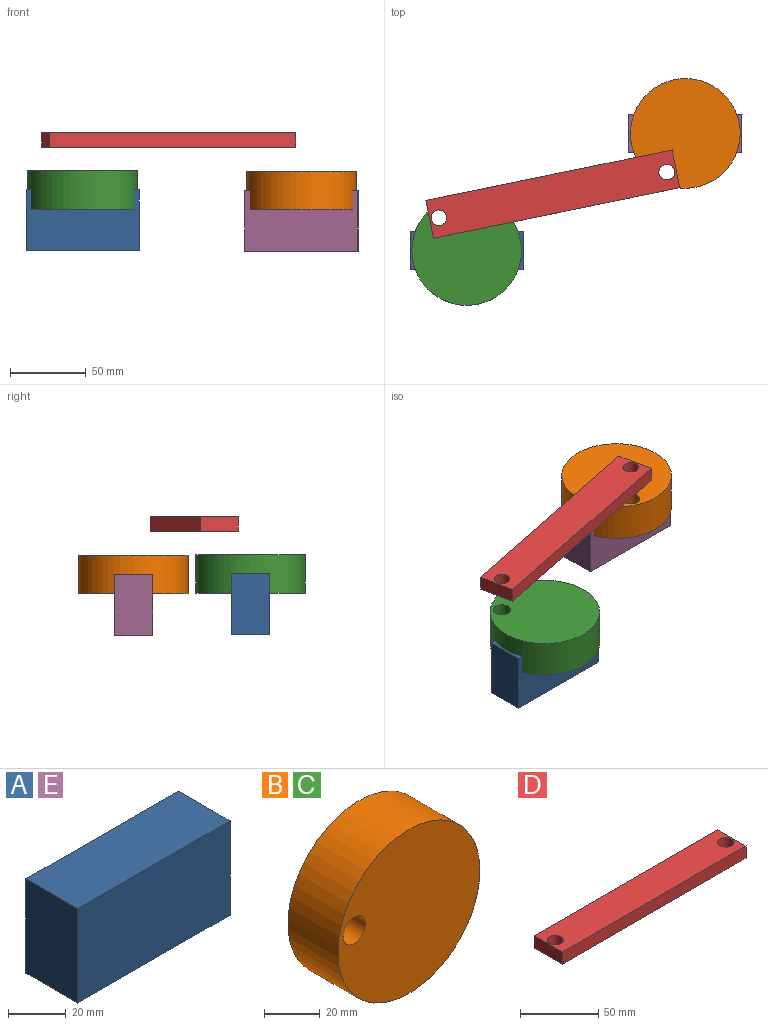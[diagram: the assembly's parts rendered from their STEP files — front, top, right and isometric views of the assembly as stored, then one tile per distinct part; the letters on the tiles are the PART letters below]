
ASSEMBLY  parts=5 mates=4
PART A: 6 faces, bbox 74.7x25.4x40 mm
  f0: plane 40.01x25.4mm, normal (-1,0,0), area 1016.1mm2, adj f1,f3,f4,f5
  f1: plane 74.7x25.4mm, normal (0,0,-1), area 1897.4mm2, adj f0,f2,f4,f5
  f2: plane 40.01x25.4mm, normal (1,0,0), area 1016.1mm2, adj f1,f3,f4,f5
  f3: plane 74.7x25.4mm, normal (0,0,1), area 1897.4mm2, adj f0,f2,f4,f5
  f4: plane 74.7x40.01mm, normal (0,-1,0), area 2988.4mm2, adj f0,f1,f2,f3
  f5: plane 74.7x40.01mm, normal (0,1,0), area 2988.4mm2, adj f0,f1,f2,f3
PART B: 4 faces, bbox 72.2x25.4x72.2 mm
  f0: cylinder r=36.12mm len=72.24mm, axis (0,1,0), area 5764.4mm2, adj f1,f2
  f1: plane 72.24x72.24mm, normal (0,-1,0), area 3994.8mm2, adj f0,f3
  f2: plane 72.24x72.24mm, normal (0,1,0), area 3994.8mm2, adj f0,f3
  f3: cylinder r=5.75mm len=25.4mm, axis (0,-1,0), area 917.4mm2, adj f1,f2
PART C: same geometry as B
PART D: 8 faces, bbox 165.7x25.4x9.5 mm
  f0: plane 25.4x9.48mm, normal (-1,0,0), area 240.8mm2, adj f1,f3,f4,f5
  f1: plane 165.67x25.4mm, normal (0,0,-1), area 4039mm2, adj f0,f2,f4,f5,f6,f7
  f2: plane 25.4x9.48mm, normal (1,0,0), area 240.8mm2, adj f1,f3,f4,f5
  f3: plane 165.67x25.4mm, normal (0,0,1), area 4039mm2, adj f0,f2,f4,f5,f6,f7
  f4: plane 165.67x9.48mm, normal (0,-1,0), area 1570.5mm2, adj f0,f1,f2,f3
  f5: plane 165.67x9.48mm, normal (0,1,0), area 1570.5mm2, adj f0,f1,f2,f3
  f6: cylinder r=5.15mm len=10.3mm, axis (0,0,-1), area 306.6mm2, adj f1,f3
  f7: cylinder r=5.22mm len=10.44mm, axis (0,0,1), area 311mm2, adj f1,f3
PART E: same geometry as A
PLACE A t=(102.78,-3.81,-0.11)mm fixed
PLACE B rot(axis=(0.82,0.41,0.41),101.5deg) t=(211.29,91.83,55.94)mm
PLACE C rot(axis=(0.77,-0.45,-0.45),105deg) t=(110.47,-19.66,56.39)mm
PLACE D rot(axis=(0,0,1),11.6deg) t=(80.72,22.55,66.93)mm
PLACE E rot(axis=(0,0,-1),0deg) t=(246.85,73.39,-0.55)mm fixed
MATE revolute C.f0 <-> A.f3  axis (0,0,1) through (77.76,-16.51,43.69)mm
MATE revolute B.f0 <-> E.f3  axis (0,0,1) through (221.82,60.69,43.24)mm
MATE cylindrical C.f3 <-> D.f6  axis (0,0,1) through (59.46,5.08,56.39)mm
MATE revolute D.f7 <-> B.f3  axis (0,0,1) through (209.64,35.16,81.34)mm
